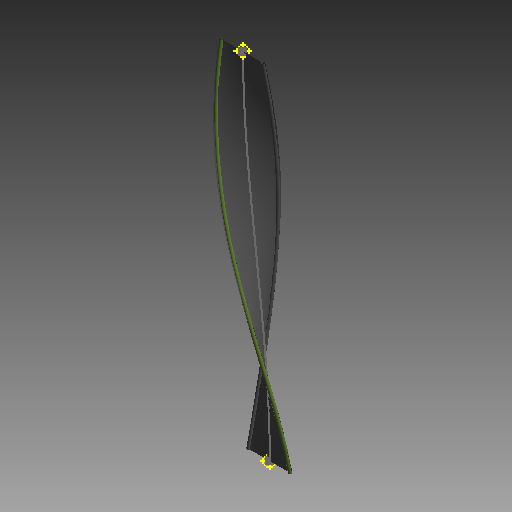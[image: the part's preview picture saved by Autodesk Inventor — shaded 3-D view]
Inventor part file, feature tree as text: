
AUTODESK INVENTOR PART (.ipt)
format: ipt  version: 2019 (Build 230136000, 136)  size: 141,312 bytes
history: native  units: mm (DEFAULTED — no unit token found)
features: other x6, sketch x3, sweep x3
ambient origin geometry x8: Origin, YZ Plane, XZ Plane, XY Plane, X Axis, Y Axis, Z Axis, Center Point
bodies: Body1 (feature_tree), Body2 (feature_tree), Body3 (feature_tree)
feature tree (12):
  other  "Work Point1"
  other  "Work Point2"
  other  "RibbonCable1"
  sketch  "Sketch1"  dims[d0=0.0mm d1=0.0mm d2=0.0mm d3=0.0mm]
  sketch  "Sketch2"  dims[d4=0.0mm d5=0.0mm]
  sketch  "Sketch3"
  other  "Srf1"
  other  "Srf2"
  other  "Srf3"
  sweep  "SweepSrf1"
  sweep  "SweepSrf2"
  sweep  "SweepSrf3"
